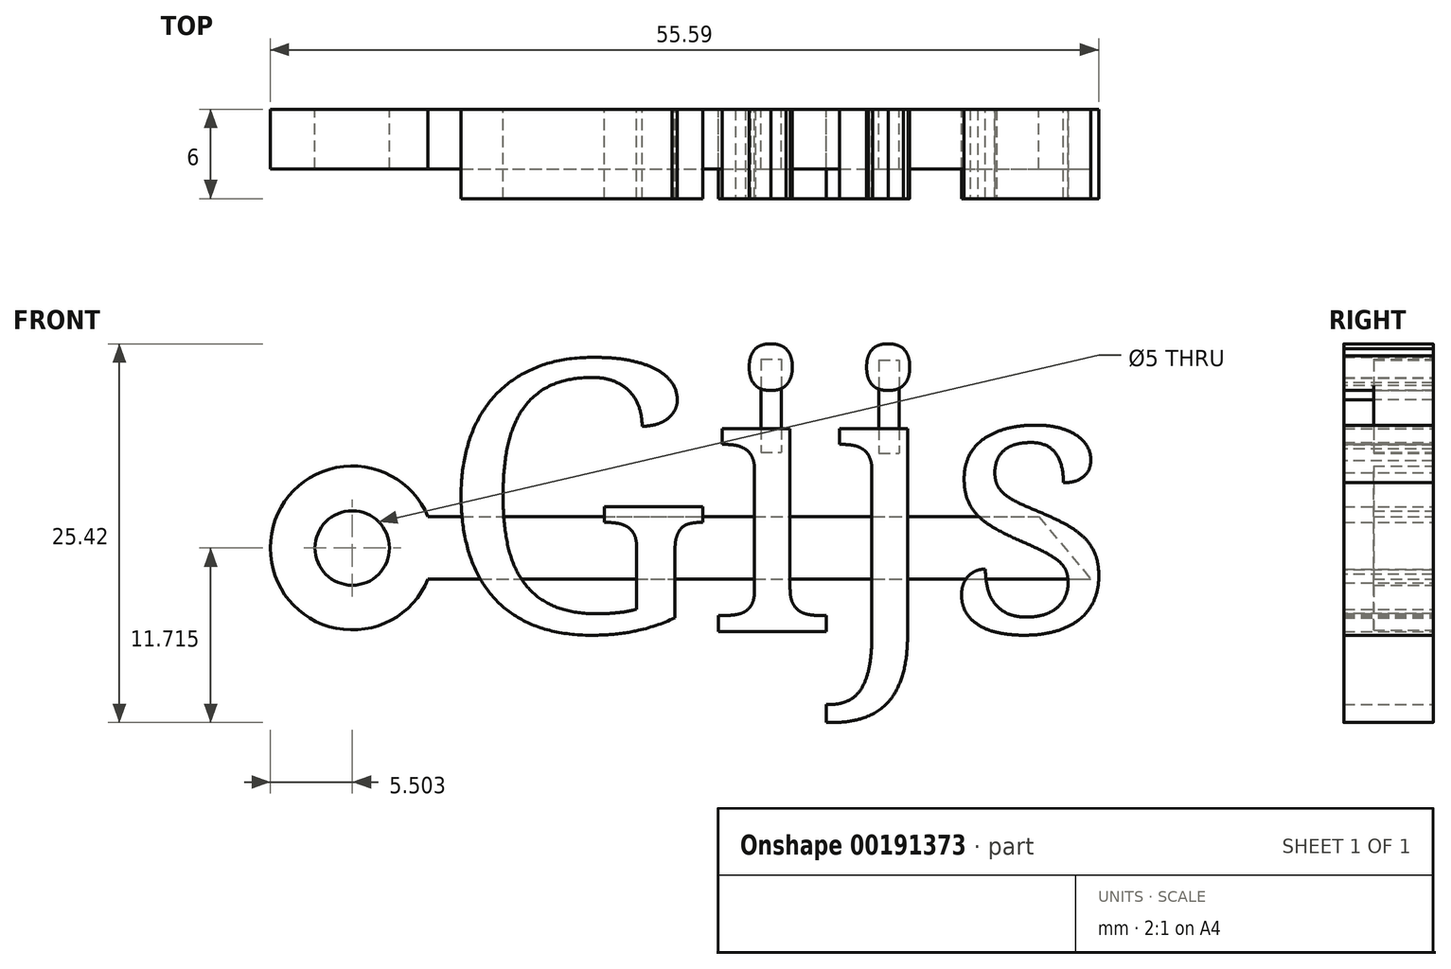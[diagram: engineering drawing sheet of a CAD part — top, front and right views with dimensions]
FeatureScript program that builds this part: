
annotation { "Feature Type Name" : "Feature", "Feature Type Description" : "" }
export const myFeature = defineFeature(function(context is Context, id is Id, definition is map)
    precondition{}
    {
        {
            var Q0;
            Q0=qCreatedBy(makeId("Front.planeOp"),FACE);
            var sketch = newSketch(context, id + "F0", { "sketchPlane" : qUnion([Q0])});
            skText(sketch, "E0", { "text": "Gijs", "fontName": "NotoSerif-Regular.ttf"});
            const initialGuessF0  = {"E0": [-0.0259, -0.011, 1, 0, 0.0183]};
            skSetInitialGuess(sketch, initialGuessF0);
            skSolve(sketch);
        }
        {
            var Q0;
            Q0 = qSketchRegion(id + "F0", true);
            extrude(context, id + "F1", {"entities" : qUnion([Q0]), "depth" : 6 * mm});
        }
        {
            var Q0;
            Q0=qCreatedBy(makeId("Front.planeOp"),FACE);
            var sketch = newSketch(context, id + "F2", { "sketchPlane" : qUnion([Q0])});
            skLineSegment(sketch, "E1.bottom", {"start": v(-26.66, -3.3) * mm, "end": v(14.32, -3.3) * mm});
            skLineSegment(sketch, "E1.top", {"start": v(-26.66, -7.5) * mm, "end": v(17.82, -7.5) * mm});
            skCircle(sketch, "E2", {"center": v(-31.75, -5.4) * mm, "radius": 2.5 * mm});
            skArc(sketch, "E3", {"start": v(-26.66, -3.3) * mm, "mid": v(-37.25, -5.4) * mm, "end": v(-26.66, -7.5) * mm});
            skPoint(sketch, "E4", {"position": v(18, -5.4) * mm});
            skLineSegment(sketch, "E5.bottom", {"start": v(-4.32, 7.27) * mm, "end": v(-2.97, 7.27) * mm});
            skLineSegment(sketch, "E5.top", {"start": v(-4.32, 1.02) * mm, "end": v(-2.97, 1.02) * mm});
            skLineSegment(sketch, "E5.left", {"start": v(-4.32, 7.27) * mm, "end": v(-4.32, 1.02) * mm});
            skLineSegment(sketch, "E5.right", {"start": v(-2.97, 7.27) * mm, "end": v(-2.97, 1.02) * mm});
            skLineSegment(sketch, "E6.bottom", {"start": v(3.6, 7.22) * mm, "end": v(4.94, 7.22) * mm});
            skLineSegment(sketch, "E6.top", {"start": v(3.6, 0.97) * mm, "end": v(4.94, 0.97) * mm});
            skLineSegment(sketch, "E6.left", {"start": v(3.6, 7.22) * mm, "end": v(3.6, 0.97) * mm});
            skLineSegment(sketch, "E6.right", {"start": v(4.94, 7.22) * mm, "end": v(4.94, 0.97) * mm});
            skLineSegment(sketch, "E7", {"start": v(14.32, -3.3) * mm, "end": v(17.82, -7.5) * mm});
            skPoint(sketch, "E8.orphan", {"position": v(18.2, -3.3) * mm});
            skSolve(sketch);
        }
        {
            var Q0;
            Q0 = qSketchRegion(id + "F2", true);
            extrude(context, id + "F3", {"entities" : qUnion([Q0]), "depth" : 4 * mm});
        }
    });
